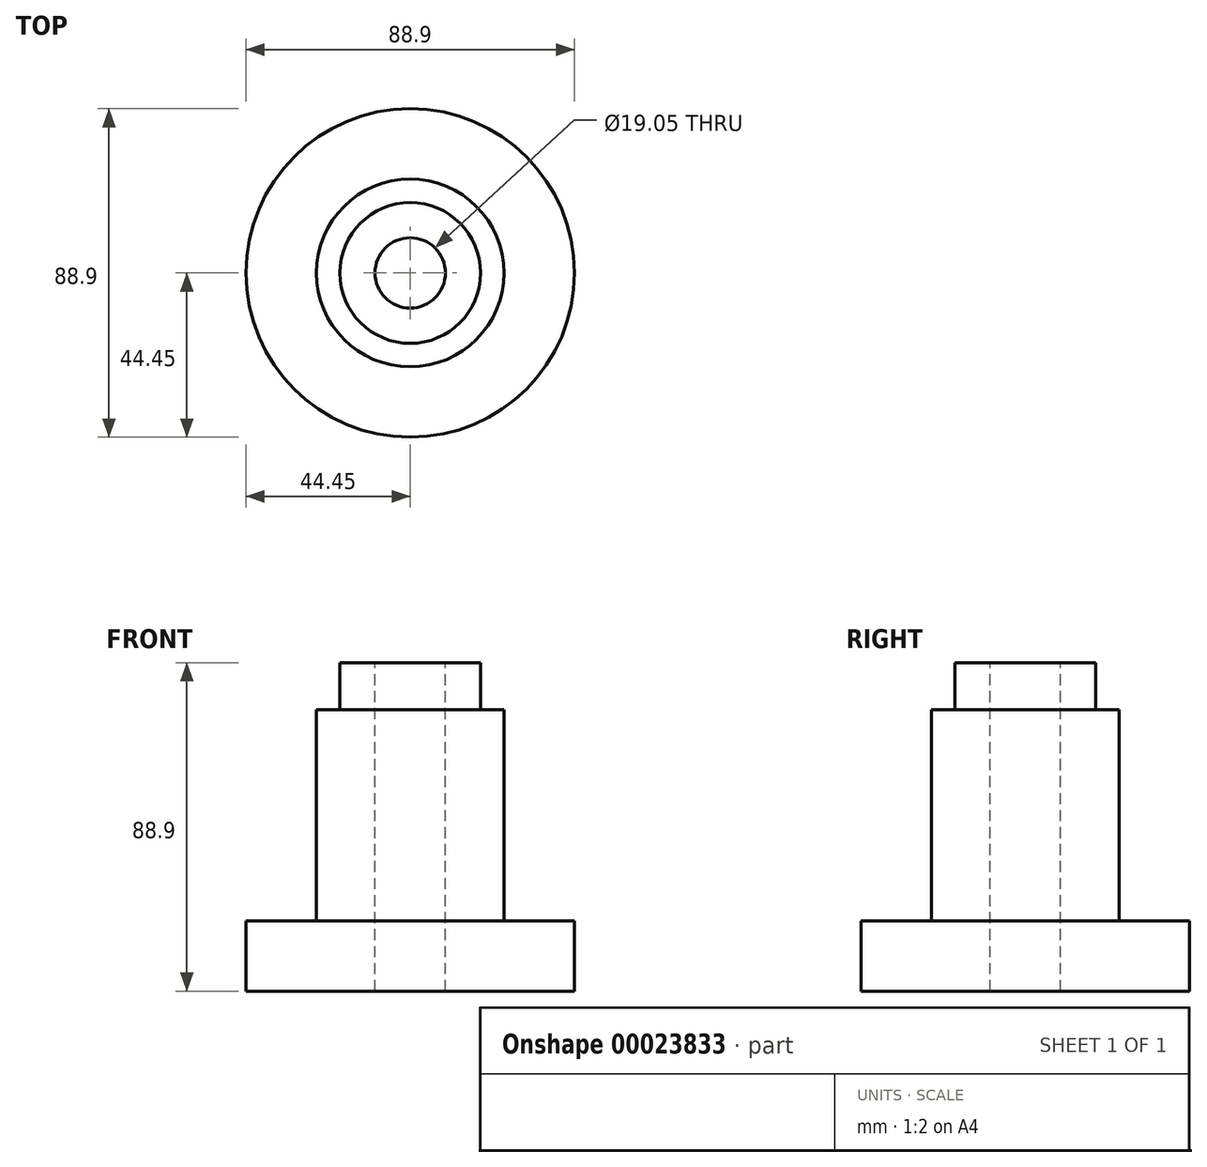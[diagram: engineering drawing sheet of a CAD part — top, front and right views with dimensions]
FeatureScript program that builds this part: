
annotation { "Feature Type Name" : "Feature", "Feature Type Description" : "" }
export const myFeature = defineFeature(function(context is Context, id is Id, definition is map)
    precondition{}
    {
        {
            var Q0;
            Q0=qCreatedBy(makeId("Front.planeOp"),FACE);
            var sketch = newSketch(context, id + "F0", { "sketchPlane" : qUnion([Q0])});
            skLineSegment(sketch, "E0", {"start": v(0, 56.49) * mm, "end": v(0, -54.9) * mm});
            skLineSegment(sketch, "E1.bottom", {"start": v(-19.05, 51.73) * mm, "end": v(-9.53, 51.73) * mm});
            skLineSegment(sketch, "E1.top", {"start": v(-19.05, 39.03) * mm, "end": v(-9.53, 39.03) * mm});
            skLineSegment(sketch, "E1.left", {"start": v(-19.05, 51.73) * mm, "end": v(-19.05, 39.03) * mm});
            skLineSegment(sketch, "E1.right", {"start": v(-9.53, 51.73) * mm, "end": v(-9.53, 39.03) * mm});
            skLineSegment(sketch, "E2.bottom", {"start": v(-9.53, 39.03) * mm, "end": v(-25.4, 39.03) * mm});
            skLineSegment(sketch, "E2.top", {"start": v(-9.52, -18.12) * mm, "end": v(-25.4, -18.12) * mm});
            skLineSegment(sketch, "E2.left", {"start": v(-9.53, 39.03) * mm, "end": v(-9.52, -18.12) * mm});
            skLineSegment(sketch, "E2.right", {"start": v(-25.4, 39.03) * mm, "end": v(-25.4, -18.12) * mm});
            skLineSegment(sketch, "E3.bottom", {"start": v(-9.52, -18.12) * mm, "end": v(-44.45, -18.12) * mm});
            skLineSegment(sketch, "E3.top", {"start": v(-9.52, -37.17) * mm, "end": v(-44.45, -37.17) * mm});
            skLineSegment(sketch, "E3.left", {"start": v(-9.52, -18.12) * mm, "end": v(-9.52, -37.17) * mm});
            skLineSegment(sketch, "E3.right", {"start": v(-44.45, -18.12) * mm, "end": v(-44.45, -37.17) * mm});
            skSolve(sketch);
        }
        {
            var Q0;
            Q0=makeQuery(id+"F0.imprint","IMPRINT",FACE,{"disambiguationData":[TD([[makeQuery(id+"F0.imprint","IMPRINT",EDGE,{"derivedFrom":sQuery(id+"F0.wireOp",EDGE,"E1.bottom")}),-1.0]])]});
            var Q1;
            Q1=makeQuery(id+"F0.imprint","IMPRINT",FACE,{"disambiguationData":[TD([[makeQuery(id+"F0.imprint","IMPRINT",EDGE,{"derivedFrom":sQuery(id+"F0.wireOp",EDGE,"E3.top")}),-1.0]])]});
            var Q2;
            {var subQ2=sQuery(id+"F0.wireOp",EDGE,"E2.left");Q2=makeQuery(id+"F0.imprint","IMPRINT",FACE,{"disambiguationData":[TD([[makeQuery(id+"F0.imprint","IMPRINT",EDGE,{"derivedFrom":subQ2}),-1.0]])]});}
            var Q3;
            Q3=sQuery(id+"F0.wireOp",EDGE,"E0");
            revolve(context, id + "F1", {"entities" : qUnion([Q0, Q1, Q2]), "axis" : qUnion([Q3]), "revolveType" : RevolveType.FULL});
        }
    });
